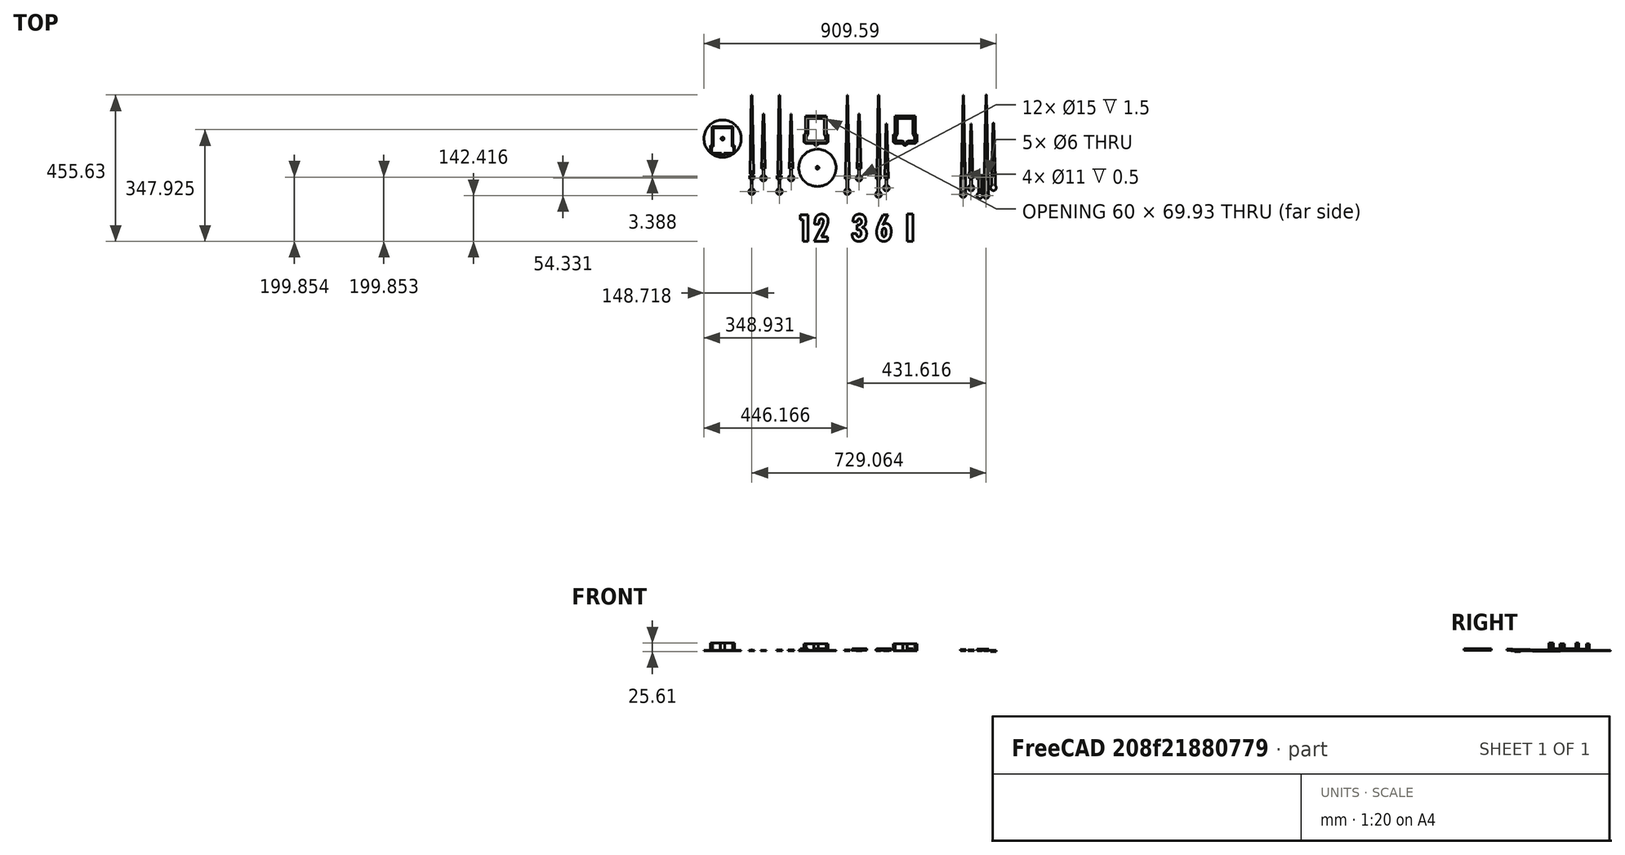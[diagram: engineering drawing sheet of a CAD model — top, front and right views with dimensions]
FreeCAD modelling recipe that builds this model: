
FCSTD DOCUMENT  (FreeCAD 0.20R29177 +426 (Git))
Label: clock
License: All rights reserved
LicenseURL: http://en.wikipedia.org/wiki/All_rights_reserved
objects: Part::Feature×45, Part::Extrusion×39, Part::Part2DObjectPython×38, Part::Cut×15, Part::MultiFuse×14, Part::Refine×9, Part::FeaturePython×7, App::DocumentObjectGroup×4
note: 167 computed .brp shape members not serialized (recipe doc carries the construction recipe); baked Part::Feature solids carry a one-line shape summary decoded from their .brp

FEATURE [Part::Feature] Fusion008002006001002001007001001
  Placement = pos=(-293.726,-1.42e-14,1.78e-14) rot=(0,0,1;0rad)
  shape: bbox 116 x 116 x 24 mm, 36 faces (baked)
FEATURE [Part::Feature] Cut001001004001001  label="clock-hourhand"
  Placement = pos=(267.524,-2.8e-14,0) rot=(0,0,1;0rad)
  shape: bbox 18 x 209 x 2 mm, 16 faces (baked)
FEATURE [Part::Feature] Cut001001007003001001
  Placement = pos=(-86.0924,0,0) rot=(0,0,1;0rad)
  shape: bbox 10.98 x 244.5 x 2.992 mm, 11 faces (baked)
FEATURE [Part::Feature] GrExplode_Slice003_solid001001  label="clock-minutehand-balancer002"
  Placement = pos=(-86.0924,0,0) rot=(0,0,1;0rad)
  shape: bbox 18 x 59.13 x 2 mm, 21 faces (baked)
FEATURE [Part::Feature] Slice002_child0001001  label="Slice002.002"
  shape: bbox 10.98 x 244.5 x 1.996 mm, 11 faces (baked)
FEATURE [Part::Feature] Fusion001001001
  shape: bbox 18 x 59.13 x 2 mm, 22 faces (baked)
FEATURE [Part::Feature] Fusion001001002001
  shape: bbox 18 x 209 x 2.002 mm, 17 faces (baked)
FEATURE [Part::Feature] Slice001_child1001001  label="Slice001.003"
  Placement = pos=(1.29731,-90.7071,-0.5) rot=(0,0,1;0rad)
  shape: bbox 116 x 116 x 1.5 mm, 4 faces (baked)
FEATURE [Part::Feature] Cut001001
  Placement = pos=(-2.79957,33.8928,-1.5) rot=(0,0,1;0rad)
  shape: bbox 75 x 91.93 x 22.5 mm, 43 faces (baked)
FEATURE [Part::Part2DObjectPython] Circle  # Draft 2D object (typed FeaturePython)
  Area = 16.7002
  FirstAngle = 0
  LastAngle = 0
  MakeFace = true
  Placement = pos=(129.41,-196.919,-3.01185) rot=(0,0,1;0rad)
  Radius = 2.30561
FEATURE [Part::Part2DObjectPython] Circle001  # Draft 2D object (typed FeaturePython)
  Area = 46.0771
  FirstAngle = 0
  LastAngle = 0
  MakeFace = true
  Placement = pos=(129.41,-196.919,-3.01185) rot=(0,0,1;0rad)
  Radius = 3.82973
FEATURE [Part::Extrusion] Extrusion
  Base = -> Circle001
  Dir = (0,2.5e-15,-0.597984)
  DirMode = 0
  FaceMakerClass = Part::FaceMakerBullseye
  LengthFwd = 0
  LengthRev = 0
  Solid = true
  Symmetric = false
FEATURE [Part::Extrusion] Extrusion001
  Base = -> Circle
  Dir = (0,2.5e-15,-0.597984)
  DirMode = 0
  FaceMakerClass = Part::FaceMakerBullseye
  LengthFwd = 0
  LengthRev = 0
  Solid = true
  Symmetric = false
FEATURE [Part::Cut] Cut
  Base = -> Extrusion
  Tool = -> Extrusion001
FEATURE [Part::Part2DObjectPython] Rectangle  # Draft 2D object (typed FeaturePython)
  Area = 586.172
  ChamferSize = 0
  Columns = 1
  FilletRadius = 0
  Height = 18.2403
  Length = 32.1361
  MakeFace = true
  Placement = pos=(115.648,-197.225,6.10831) rot=(-1,0,0;1.5708rad)
  Rows = 1
FEATURE [Part::FeaturePython] Slice  # WARN: FeaturePython — macro-defined, semantics opaque (R4)
  Base = -> Cut
  Mode = 1
  Tolerance = 0
  Tools = -> [Rectangle]
FEATURE [Part::FeaturePython] Slice_child1  label="Slice.1"  # WARN: FeaturePython — macro-defined, semantics opaque (R4)
  Base = -> Slice
  FilterType = 1
  Invert = false
  OverrideMaxVal = 0
  WindowFrom = 80
  WindowTo = 100
  items = 1
FEATURE [Part::MultiFuse] Fusion
  Shapes = -> [Fusion001001001,Slice_child1]
FEATURE [App::DocumentObjectGroup] GrExplode_Slice  label="Exploded Slice"
  Group = -> [Fusion]
FEATURE [Part::Refine] Fusion008002006001002001007001002
  Source = -> Fusion
FEATURE [Part::Feature] Fusion008002006001002001007001002001
  shape: bbox 18 x 59.13 x 2 mm, 24 faces (baked)
FEATURE [Part::Part2DObjectPython] Line  # Draft 2D object (typed FeaturePython)
  Area = 0
  ChamferSize = 0
  Closed = false
  End = (123.92,-195.225,-2.60983)
  FilletRadius = 0
  Length = 1
  MakeFace = true
  Placement = pos=(123.92,-195.225,-3.60983) rot=(-1,0,0;1.5708rad)
  Points = (2) [(0,0,0),(0,-1,-2.27374e-13)]
  Start = (123.92,-195.225,-3.60983)
  Subdivisions = 0
FEATURE [Part::Feature] Face
  shape: bbox 14 x 10.13 x 7e-07 mm, 1 faces, 0 solids (baked)
FEATURE [Part::Extrusion] Extrusion002
  Base = -> Face
  Dir = (0,-2e-15,0.402016)
  DirMode = 0
  FaceMakerClass = Part::FaceMakerBullseye
  LengthFwd = 0
  LengthRev = 0
  Solid = true
  Symmetric = false
FEATURE [Part::Feature] Face001
  shape: bbox 18 x 18 x 7e-07 mm, 1 faces, 0 solids (baked)
FEATURE [Part::Extrusion] Extrusion003
  Base = -> Face001
  Dir = (0,0,0.402016)
  DirMode = 0
  FaceMakerClass = Part::FaceMakerBullseye
  LengthFwd = 0
  LengthRev = 0
  Solid = true
  Symmetric = false
FEATURE [Part::MultiFuse] Fusion008002006001002001007001002002
  Shapes = -> [Extrusion002,Extrusion003,Fusion008002006001002001007001002001]
FEATURE [Part::Refine] Fusion008002006001002001007001002002001
  Source = -> Fusion008002006001002001007001002002
FEATURE [Part::Feature] Fusion008002006001002001007001002002001001
  shape: bbox 18 x 59.13 x 2.402 mm, 24 faces (baked)
FEATURE [Part::Feature] Face002
  shape: bbox 18 x 18 x 2e-07 mm, 1 faces, 0 solids (baked)
FEATURE [Part::Extrusion] Extrusion004
  Base = -> Face002
  Dir = (-1e-16,0,0.391829)
  DirMode = 0
  FaceMakerClass = Part::FaceMakerBullseye
  LengthFwd = 0
  LengthRev = 0
  Solid = true
  Symmetric = false
FEATURE [Part::MultiFuse] Fusion008002006001002001007001002002001002
  Shapes = -> [Fusion001001002001,Extrusion004]
FEATURE [Part::Refine] Fusion008002006001002001007001002002001002001
  Source = -> Fusion008002006001002001007001002002001002
FEATURE [Part::Feature] Fusion008002006001002001007001002002001002001001
  shape: bbox 18 x 209 x 2.392 mm, 17 faces (baked)
FEATURE [Part::Feature] Fusion008002006001002001007001002002001002001002
  Placement = pos=(211.355,-1.42e-14,4e-14) rot=(0,0,1;0rad)
  shape: bbox 18 x 59.13 x 2.402 mm, 24 faces (baked)
FEATURE [Part::Feature] Slice002_child0001002  label="Slice002.003"
  Placement = pos=(211.355,-1.42e-14,4e-14) rot=(0,0,1;0rad)
  shape: bbox 10.98 x 244.5 x 1.996 mm, 11 faces (baked)
FEATURE [Part::Feature] Fusion008002006001002001007001002002001002001003
  Placement = pos=(211.355,-1.42e-14,4e-14) rot=(0,0,1;0rad)
  shape: bbox 18 x 209 x 2.392 mm, 17 faces (baked)
FEATURE [Part::Part2DObjectPython] Circle002  # Draft 2D object (typed FeaturePython)
  Area = 38.4845
  FirstAngle = 0
  LastAngle = 0
  MakeFace = true
  Placement = pos=(377.064,-163.449,-3) rot=(0,0,1;0rad)
  Radius = 3.5
FEATURE [Part::Extrusion] Extrusion005
  Base = -> Circle002
  Dir = (0,0,-9.31719)
  DirMode = 0
  FaceMakerClass = Part::FaceMakerBullseye
  LengthFwd = 0
  LengthRev = 0
  Solid = true
  Symmetric = false
FEATURE [Part::Cut] Cut001001007003001002
  Base = -> Fusion008002006001002001007001002002001002001003
  Tool = -> Extrusion005
FEATURE [Part::Part2DObjectPython] Circle003  # Draft 2D object (typed FeaturePython)
  Area = 15.2053
  FirstAngle = 0
  LastAngle = 0
  MakeFace = true
  Placement = pos=(340.766,-184.928,-3.01297) rot=(0,0,1;0rad)
  Radius = 2.2
FEATURE [Part::Extrusion] Extrusion006
  Base = -> Circle003
  Dir = (0,0,-7.79458)
  DirMode = 0
  FaceMakerClass = Part::FaceMakerBullseye
  LengthFwd = 0
  LengthRev = 0
  Solid = true
  Symmetric = false
FEATURE [Part::Cut] Cut001001007003001003
  Base = -> Slice002_child0001002
  Tool = -> Extrusion006
FEATURE [Part::Feature] Face003
  shape: bbox 4.611 x 4.611 x 2e-07 mm, 1 faces, 0 solids (baked)
FEATURE [Part::Extrusion] Extrusion007
  Base = -> Face003
  Dir = (0,0,-0.996429)
  DirMode = 0
  FaceMakerClass = Part::FaceMakerBullseye
  LengthFwd = 0
  LengthRev = 0
  Solid = true
  Symmetric = false
FEATURE [Part::Cut] Cut001001007003001004
  Base = -> Cut001001007003001003
  Tool = -> Extrusion007
FEATURE [Part::Part2DObjectPython] Rectangle001  # Draft 2D object (typed FeaturePython)
  Area = 148.077
  ChamferSize = 0
  Columns = 1
  FilletRadius = 0
  Height = 11.1933
  Length = 13.229
  MakeFace = true
  Placement = pos=(335.406,-182.807,-10.6052) rot=(0.57735,-0.57735,-0.57735;2.0944rad)
  Rows = 1
FEATURE [Part::Part2DObjectPython] Rectangle002  # Draft 2D object (typed FeaturePython)
  Area = 215.213
  ChamferSize = 0
  Columns = 1
  FilletRadius = 0
  Height = 15.7464
  Length = 13.6675
  MakeFace = true
  Placement = pos=(346.125,-182.807,-12.8817) rot=(0.57735,-0.57735,-0.57735;2.0944rad)
  Rows = 1
FEATURE [Part::FeaturePython] Slice001  # WARN: FeaturePython — macro-defined, semantics opaque (R4)
  Base = -> Cut001001007003001004
  Mode = 1
  Tolerance = 0
  Tools = -> [Rectangle002]
FEATURE [Part::FeaturePython] Slice001_child1  label="Slice001.1"  # WARN: FeaturePython — macro-defined, semantics opaque (R4)
  Base = -> Slice001
  FilterType = 1
  Invert = false
  OverrideMaxVal = 0
  WindowFrom = 80
  WindowTo = 100
  items = 1
FEATURE [App::DocumentObjectGroup] GrExplode_Slice001  label="Exploded Slice001"
  Group = -> [Slice001_child1]
FEATURE [Part::FeaturePython] Slice002  # WARN: FeaturePython — macro-defined, semantics opaque (R4)
  Base = -> Slice001_child1
  Mode = 1
  Tolerance = 0
  Tools = -> [Rectangle001]
FEATURE [Part::FeaturePython] Slice002_child0  label="Slice002.0"  # WARN: FeaturePython — macro-defined, semantics opaque (R4)
  Base = -> Slice002
  FilterType = 1
  Invert = false
  OverrideMaxVal = 0
  WindowFrom = 80
  WindowTo = 100
  items = 0
FEATURE [App::DocumentObjectGroup] GrExplode_Slice002  label="Exploded Slice002"
  Group = -> [Slice002_child0]
FEATURE [Part::Part2DObjectPython] Circle004  # Draft 2D object (typed FeaturePython)
  Area = 16.619
  FirstAngle = 0
  LastAngle = 0
  MakeFace = true
  Placement = pos=(340.766,-196.919,-2.60983) rot=(1,0,0;3.14167rad)
  Radius = 2.3
FEATURE [Part::Feature] Face005
  Placement = pos=(211.355,-1.42e-14,4e-14) rot=(0,0,1;0rad)
  shape: bbox 4.694 x 7e-07 x 2.4 mm, 1 faces, 0 solids (baked)
FEATURE [Part::Extrusion] Extrusion008
  Base = -> Face005
  Dir = (1.62e-14,3.80561,9.57e-14)
  DirMode = 0
  FaceMakerClass = Part::FaceMakerBullseye
  LengthFwd = 0
  LengthRev = 0
  Solid = true
  Symmetric = false
FEATURE [Part::Feature] Face006
  Placement = pos=(211.355,-1.42e-14,4e-14) rot=(0,0,1;0rad)
  shape: bbox 4.694 x 7e-07 x 2.4 mm, 1 faces, 0 solids (baked)
FEATURE [Part::Extrusion] Extrusion009
  Base = -> Face006
  Dir = (-1.43e-14,3.80561,4.6e-14)
  DirMode = 0
  FaceMakerClass = Part::FaceMakerBullseye
  LengthFwd = 0
  LengthRev = 0
  Solid = true
  Symmetric = false
FEATURE [Part::Extrusion] Extrusion010
  Base = -> Circle004
  Dir = (-1.407e-13,0.00235422,-31.7358)
  DirMode = 0
  FaceMakerClass = Part::FaceMakerBullseye
  LengthFwd = 0
  LengthRev = 0
  Placement = pos=(5.7e-14,-0.00117711,15.8679) rot=(0,0,1;0rad)
  Solid = true
  Symmetric = false
FEATURE [Part::Feature] Face007
  shape: bbox 7e-07 x 3.806 x 1 mm, 1 faces, 0 solids (baked)
FEATURE [Part::Extrusion] Extrusion011
  Base = -> Face007
  Dir = (-4.61123,1.96e-14,1.3e-15)
  DirMode = 0
  FaceMakerClass = Part::FaceMakerBullseye
  LengthFwd = 0
  LengthRev = 0
  Solid = true
  Symmetric = false
FEATURE [Part::Feature] Face008
  Placement = pos=(211.355,-1.42e-14,4e-14) rot=(0,0,1;0rad)
  shape: bbox 7e-07 x 2 x 1 mm, 1 faces, 0 solids (baked)
FEATURE [Part::Extrusion] Extrusion012
  Base = -> Face008
  Dir = (-4.61123,1.3e-14,-1.25e-14)
  DirMode = 0
  FaceMakerClass = Part::FaceMakerBullseye
  LengthFwd = 0
  LengthRev = 0
  Solid = true
  Symmetric = false
FEATURE [Part::MultiFuse] Fusion008002006001002001007001002002001002001004
  Shapes = -> [Extrusion012,Extrusion011,Extrusion008,Extrusion009,Fusion008002006001002001007001002002001002001002]
FEATURE [Part::Part2DObjectPython] Circle005  # Draft 2D object (typed FeaturePython)
  Area = 95.0332
  FirstAngle = 0
  LastAngle = 0
  MakeFace = true
  Placement = pos=(340.766,-196.919,-2.60983) rot=(0,0,1;0rad)
  Radius = 5.5
FEATURE [Part::Cut] Cut001001007003001005
  Base = -> Fusion008002006001002001007001002002001002001004
  Tool = -> Extrusion010
FEATURE [Part::Extrusion] Extrusion013
  Base = -> Circle005
  Dir = (0,2.5e-15,-0.5)
  DirMode = 0
  FaceMakerClass = Part::FaceMakerBullseye
  LengthFwd = 0
  LengthRev = 0
  Solid = true
  Symmetric = false
FEATURE [Part::Cut] Cut001001007003001006
  Base = -> Cut001001007003001005
  Tool = -> Extrusion013
FEATURE [Part::Refine] Cut001001007003001006001
  Source = -> Cut001001007003001006
FEATURE [Part::Feature] Face009
  shape: bbox 14 x 7e-07 x 2.4 mm, 1 faces, 0 solids (baked)
FEATURE [Part::Extrusion] Extrusion014
  Base = -> Face009
  Dir = (1.3e-15,0.4,5.7e-15)
  DirMode = 0
  FaceMakerClass = Part::FaceMakerBullseye
  LengthFwd = 0
  LengthRev = 0
  Solid = true
  Symmetric = false
FEATURE [Part::MultiFuse] Fusion008002006001002001007001002002001002001005
  Shapes = -> [Extrusion014,Cut001001007003001006001]
FEATURE [Part::Part2DObjectPython] Line004  # Draft 2D object (typed FeaturePython)
  Area = 0
  ChamferSize = 0
  Closed = false
  End = (346.256,-191.019,-2.60983)
  FilletRadius = 0
  Length = 1
  MakeFace = true
  Placement = pos=(346.256,-191.019,-3.60983) rot=(-1,0,0;1.5708rad)
  Points = (2) [(0,0,0),(0,-1,1.13687e-13)]
  Start = (346.256,-191.019,-3.60983)
  Subdivisions = 0
FEATURE [Part::Part2DObjectPython] Line005  # Draft 2D object (typed FeaturePython)
  Area = 0
  ChamferSize = 0
  Closed = false
  End = (335.275,-191.019,-2.60983)
  FilletRadius = 0
  Length = 1
  MakeFace = true
  Placement = pos=(335.275,-191.019,-3.60983) rot=(-1,0,0;1.5708rad)
  Points = (2) [(0,0,0),(0,-1,1.13687e-13)]
  Start = (335.275,-191.019,-3.60983)
  Subdivisions = 0
FEATURE [Part::Part2DObjectPython] Line007  # Draft 2D object (typed FeaturePython)
  Area = 0
  ChamferSize = 0
  Closed = false
  End = (333.766,-196.918,-2.60983)
  FilletRadius = 0
  Length = 6.08928
  MakeFace = true
  Placement = pos=(335.275,-191.019,-2.60983) rot=(0,0,1;0rad)
  Points = (2) [(0,0,0),(-1.50938,-5.89925,-4.08562e-14)]
  Start = (335.275,-191.019,-2.60983)
  Subdivisions = 0
FEATURE [Part::Part2DObjectPython] Line009  # Draft 2D object (typed FeaturePython)
  Area = 0
  ChamferSize = 0
  Closed = false
  End = (346.256,-191.019,-2.60983)
  FilletRadius = 0
  Length = 6.08928
  MakeFace = true
  Placement = pos=(347.766,-196.918,-2.60983) rot=(0,0,1;0rad)
  Points = (2) [(0,0,0),(-1.50937,5.89925,3.55271e-15)]
  Start = (347.766,-196.918,-2.60983)
  Subdivisions = 0
FEATURE [Part::Part2DObjectPython] Wire  # Draft 2D object (typed FeaturePython)
  Area = 4.45209
  ChamferSize = 0
  Closed = true
  End = (333.766,-191.019,-2.60983)
  FilletRadius = 0
  Length = 13.4979
  MakeFace = true
  Placement = pos=(333.766,-196.918,-2.60983) rot=(0,0,1;0rad)
  Points = (3) [(0,0,0),(1.50938,5.89925,4.17444e-14),(0,5.89925,2.66454e-14)]
  Start = (333.766,-196.918,-2.60983)
  Subdivisions = 0
FEATURE [Part::Extrusion] Extrusion015
  Base = -> Wire
  Dir = (1.197e-13,1.354e-13,-11.1843)
  DirMode = 0
  FaceMakerClass = Part::FaceMakerBullseye
  LengthFwd = 0
  LengthRev = 0
  Solid = true
  Symmetric = false
FEATURE [Part::Cut] Cut001001007003001006002
  Base = -> Fusion008002006001002001007001002002001002001005
  Tool = -> Extrusion015
FEATURE [Part::Part2DObjectPython] Wire001  # Draft 2D object (typed FeaturePython)
  Area = 4.45209
  ChamferSize = 0
  Closed = true
  End = (347.766,-191.019,-2.60983)
  FilletRadius = 0
  Length = 13.4979
  MakeFace = true
  Placement = pos=(347.766,-196.918,-2.60983) rot=(0,0,1;0rad)
  Points = (3) [(0,0,0),(-1.50937,5.89925,4.44089e-15),(0,5.89925,-2.22045e-15)]
  Start = (347.766,-196.918,-2.60983)
  Subdivisions = 0
FEATURE [Part::Extrusion] Extrusion016
  Base = -> Wire001
  Dir = (-6.82e-14,1.324e-13,-18.3507)
  DirMode = 0
  FaceMakerClass = Part::FaceMakerBullseye
  LengthFwd = 0
  LengthRev = 0
  Solid = true
  Symmetric = false
FEATURE [Part::Cut] Cut001001007003001006003
  Base = -> Cut001001007003001006002
  Tool = -> Extrusion016
FEATURE [Part::Part2DObjectPython] Rectangle003  # Draft 2D object (typed FeaturePython)
  Area = 74.4926
  ChamferSize = 0
  Columns = 1
  FilletRadius = 0
  Height = 2.48841
  Length = 29.9358
  MakeFace = true
  Placement = pos=(322.609,-190.33,-5.00983) rot=(1,0,0;3.14159rad)
  Rows = 1
FEATURE [Part::Extrusion] Extrusion017
  Base = -> Rectangle003
  Dir = (-1e-15,-1e-15,1.4)
  DirMode = 0
  FaceMakerClass = Part::FaceMakerBullseye
  LengthFwd = 0
  LengthRev = 0
  Solid = true
  Symmetric = false
FEATURE [Part::Cut] Cut001001007003001006004
  Base = -> Cut001001007003001006003
  Tool = -> Extrusion017
FEATURE [Part::Refine] Slice002_child0001003  label="Slice002.004"
  Source = -> Slice002_child0
FEATURE [Part::Refine] Cut001001007003001006004001
  Source = -> Cut001001007003001006004
FEATURE [Part::Part2DObjectPython] Circle006  # Draft 2D object (typed FeaturePython)
  Area = 15.2053
  FirstAngle = 0
  LastAngle = 0
  MakeFace = true
  Placement = pos=(340.766,-184.928,-4.0094) rot=(1,0,0;7.4e-05rad)
  Radius = 2.2
FEATURE [Part::Part2DObjectPython] Circle007  # Draft 2D object (typed FeaturePython)
  Area = 78.5398
  FirstAngle = 0
  LastAngle = 0
  MakeFace = true
  Placement = pos=(340.766,-184.928,-4.0094) rot=(1,0,0;7.4e-05rad)
  Radius = 5
FEATURE [Part::Part2DObjectPython] Circle008  # Draft 2D object (typed FeaturePython)
  Area = 28.2743
  FirstAngle = 0
  LastAngle = 0
  MakeFace = true
  Placement = pos=(340.766,-196.918,-3.10983) rot=(0,0,1;0rad)
  Radius = 3
FEATURE [Part::Extrusion] Extrusion020
  Base = -> Circle008
  Dir = (1e-16,2.86e-14,-5.71518)
  DirMode = 0
  FaceMakerClass = Part::FaceMakerBullseye
  LengthFwd = 0
  LengthRev = 0
  Solid = true
  Symmetric = false
FEATURE [Part::Cut] Cut001001007003001006004003
  Base = -> Cut001001007003001006004001
  Tool = -> Extrusion020
FEATURE [Part::Part2DObjectPython] Wire003  # Draft 2D object (typed FeaturePython)
  Area = 1509.1
  ChamferSize = 0
  Closed = true
  End = (341.766,54.5638,-3.99126)
  FilletRadius = 0
  Length = 487.383
  MakeFace = true
  Placement = pos=(346.125,-182.728,-4.00924) rot=(1,0,0;7.4e-05rad)
  Points = (4) [(0,0,0),(-10.7193,8.52651e-14,-3.77476e-14),(-6.35968,237.292,0.000371511),(-4.35968,237.292,0.000371511)]
  Start = (346.125,-182.728,-4.00924)
  Subdivisions = 0
FEATURE [Part::Extrusion] Extrusion021
  Base = -> Wire003
  Dir = (-5.3e-15,7.56942e-05,-0.999295)
  DirMode = 0
  FaceMakerClass = Part::FaceMakerBullseye
  LengthFwd = 0
  LengthRev = 0
  Solid = true
  Symmetric = false
FEATURE [Part::Part2DObjectPython] Rectangle006  # Draft 2D object (typed FeaturePython)
  Area = 77.266
  ChamferSize = 0
  Columns = 1
  FilletRadius = 0
  Height = 7.2081
  Length = 10.7193
  MakeFace = true
  Placement = pos=(335.406,-189.936,-4.0094) rot=(1,0,0;7.6e-05rad)
  Rows = 1
FEATURE [Part::Extrusion] Extrusion022
  Base = -> Rectangle006
  Dir = (-5.3e-15,7.57232e-05,-0.999678)
  DirMode = 0
  FaceMakerClass = Part::FaceMakerBullseye
  LengthFwd = 0
  LengthRev = 0
  Solid = true
  Symmetric = false
FEATURE [Part::Part2DObjectPython] Circle009  # Draft 2D object (typed FeaturePython)
  Area = 15.2053
  FirstAngle = 0
  LastAngle = 0
  MakeFace = true
  Placement = pos=(340.766,-184.928,-4.0094) rot=(1,0,0;7.6e-05rad)
  Radius = 2.2
FEATURE [Part::Extrusion] Extrusion023
  Base = -> Circle009
  Dir = (-3.72e-14,0.000537769,-7.09948)
  DirMode = 0
  FaceMakerClass = Part::FaceMakerBullseye
  LengthFwd = 0
  LengthRev = 0
  Placement = pos=(5.7e-14,-0.000268884,3.54974) rot=(0,0,1;0rad)
  Solid = true
  Symmetric = false
FEATURE [Part::MultiFuse] Fusion008002006001002001007001002002001002001007
  Shapes = -> [Extrusion021,Extrusion022]
FEATURE [Part::Cut] Cut001001007003001006004004
  Base = -> Fusion008002006001002001007001002002001002001007
  Tool = -> Extrusion023
FEATURE [Part::Part2DObjectPython] Circle010  # Draft 2D object (typed FeaturePython)
  Area = 28.2743
  FirstAngle = 0
  LastAngle = 0
  MakeFace = true
  Placement = pos=(340.766,-184.928,-4.00902) rot=(1,0,0;7.6e-05rad)
  Radius = 3
FEATURE [Part::Extrusion] Extrusion024
  Base = -> Circle010
  Dir = (-1.6e-15,2.27487e-05,-0.300322)
  DirMode = 0
  FaceMakerClass = Part::FaceMakerBullseye
  LengthFwd = 0
  LengthRev = 0
  Solid = true
  Symmetric = false
FEATURE [Part::Cut] Cut001001007003001006004005
  Base = -> Cut001001007003001006004004
  Tool = -> Extrusion024
FEATURE [Part::Refine] Cut001001007003001006004005001
  Source = -> Cut001001007003001006004005
FEATURE [Part::Part2DObjectPython] Circle011  # Draft 2D object (typed FeaturePython)
  Area = 30.1907
  FirstAngle = 0
  LastAngle = 0
  MakeFace = true
  Placement = pos=(340.766,-184.928,-4.00902) rot=(1,0,0;7.6e-05rad)
  Radius = 3.1
FEATURE [Part::Extrusion] Extrusion025
  Base = -> Circle011
  Dir = (-1.6e-15,2.27487e-05,-0.300322)
  DirMode = 0
  FaceMakerClass = Part::FaceMakerBullseye
  LengthFwd = 0
  LengthRev = 0
  Solid = true
  Symmetric = false
FEATURE [Part::Cut] Cut001001007003001006004005002
  Base = -> Cut001001007003001006004005001
  Tool = -> Extrusion025
FEATURE [Part::Part2DObjectPython] Circle012  # Draft 2D object (typed FeaturePython)
  Area = 39.5919
  FirstAngle = 0
  LastAngle = 0
  MakeFace = true
  Placement = pos=(377.064,-163.449,-4.00083) rot=(0,0,1;0rad)
  Radius = 3.55
FEATURE [Part::Extrusion] Extrusion026
  Base = -> Circle012
  Dir = (6.1e-15,1.6e-15,-19.7391)
  DirMode = 0
  FaceMakerClass = Part::FaceMakerBullseye
  LengthFwd = 0
  LengthRev = 0
  Solid = true
  Symmetric = false
FEATURE [Part::Cut] Cut001001007003001006004005003
  Base = -> Cut001001007003001002
  Tool = -> Extrusion026
FEATURE [Part::Feature] Cut001001007003001006004005003001  label="HourHand"
  shape: bbox 18 x 209 x 2.392 mm, 15 faces (baked)
FEATURE [Part::Feature] Cut001001007003001006004005002001  label="MinuteHand"
  shape: bbox 10.72 x 244.5 x 1.018 mm, 15 faces (baked)
FEATURE [Part::Feature] Cut001001007003001006004003001  label="MinuteHand-Balance"
  shape: bbox 18 x 63.34 x 2.402 mm, 25 faces (baked)
FEATURE [Part::Feature] Fusion008002006001002001007001002002001002001008  label="HourHand.v2"
  Placement = pos=(85.2168,-30.8568,1.38283) rot=(0,0,1;0rad)
  shape: bbox 18 x 209 x 2.392 mm, 14 faces (baked)
FEATURE [Part::Feature] Fusion008002006001002001007001002002001002001009  label="MinuteHand-Balance.v2"
  Placement = pos=(96.782,0,6.6e-14) rot=(0,0,1;0rad)
  shape: bbox 18 x 72.34 x 3.801 mm, 25 faces (baked)
FEATURE [Part::Feature] Cut001001007003001006004005003002  label="MinuteHand.v2"
  Placement = pos=(97.1955,-0.0933249,-0.000752062) rot=(0,0,1;0rad)
  shape: bbox 10.72 x 244.5 x 1.018 mm, 15 faces (baked)
FEATURE [Part::Feature] Cut001001007003001006004005003004_solid001001  label="Cut001001007003001006004005003004 (Solid)002"
  Placement = pos=(276.655,-2.8e-14,-6.9e-14) rot=(0,0,1;0rad)
  shape: bbox 73.5 x 91.93 x 21.5 mm, 45 faces (baked)
FEATURE [App::DocumentObjectGroup] Draft_Construction  label="Construction"
FEATURE [Part::Part2DObjectPython] ShapeString  # Draft 2D object (typed FeaturePython)
  FontFile = /run/user/1000/doc/f5ed1d15/Futura Bold font.ttf
  MakeFace = true
  Placement = pos=(183.377,-400.159,-3.5) rot=(0,0,1;0rad)
  Size = 93
  String = 12
  Tracking = 0
FEATURE [Part::Part2DObjectPython] ShapeString001  # Draft 2D object (typed FeaturePython)
  FontFile = /run/user/1000/doc/f5ed1d15/Futura Bold font.ttf
  MakeFace = true
  Placement = pos=(183.377,-486.508,-3.5) rot=(0,0,1;0rad)
  Size = 93
  String = 3
  Tracking = 0
FEATURE [Part::Part2DObjectPython] Line012  # Draft 2D object (typed FeaturePython)
  Area = 0
  ChamferSize = 0
  Closed = false
  End = (528.923,-400.159,-3.5)
  FilletRadius = 0
  Length = 350
  MakeFace = true
  Placement = pos=(178.923,-400.159,-3.5) rot=(0,0,1;0rad)
  Points = (2) [(0,0,0),(350,0,0)]
  Start = (178.923,-400.159,-3.5)
  Subdivisions = 0
FEATURE [Part::Part2DObjectPython] Rectangle007  # Draft 2D object (typed FeaturePython)
  Area = 1599.7
  ChamferSize = 0
  Columns = 1
  FilletRadius = 0
  Height = 85
  Length = 18.82
  MakeFace = true
  Placement = pos=(377.158,-400.159,-3.5) rot=(0,0,1;0rad)
  Rows = 1
FEATURE [Part::Extrusion] Extrusion027
  Base = -> ShapeString
  Dir = (0,0,3)
  DirMode = 0
  FaceMakerClass = Part::FaceMakerBullseye
  LengthFwd = 0
  LengthRev = 0
  Solid = true
  Symmetric = false
FEATURE [Part::Extrusion] Extrusion028
  Base = -> ShapeString001
  Dir = (0,0,3)
  DirMode = 0
  FaceMakerClass = Part::FaceMakerBullseye
  LengthFwd = 0
  LengthRev = 0
  Placement = pos=(169.403,86.3489,0) rot=(0,0,1;0rad)
  Solid = true
  Symmetric = false
FEATURE [Part::Extrusion] Extrusion029
  Base = -> Rectangle007
  Dir = (0,0,3)
  DirMode = 0
  FaceMakerClass = Part::FaceMakerBullseye
  LengthFwd = 0
  LengthRev = 0
  Placement = pos=(149.284,7.3953e-11,0) rot=(0,0,1;0rad)
  Solid = true
  Symmetric = false
FEATURE [Part::Part2DObjectPython] ShapeString002  # Draft 2D object (typed FeaturePython)
  FontFile = /run/user/1000/doc/f5ed1d15/Futura Bold font.ttf
  MakeFace = true
  Placement = pos=(183.377,-486.508,-3.5) rot=(0,0,1;0rad)
  Size = 93
  String = 6
  Tracking = 0
FEATURE [Part::Extrusion] Extrusion030
  Base = -> ShapeString002
  Dir = (0,0,3)
  DirMode = 0
  FaceMakerClass = Part::FaceMakerBullseye
  LengthFwd = 0
  LengthRev = 0
  Placement = pos=(245.378,86.3489,0) rot=(0,0,1;0rad)
  Solid = true
  Symmetric = false
FEATURE [Part::Feature] Fusion008002006001002001007001002002001002001010001001
  Placement = pos=(263.433,-1.42e-14,-1.4331e-12) rot=(0,0,1;0rad)
  shape: bbox 10.72 x 244.5 x 2.012 mm, 20 faces, 2 solids (baked)
FEATURE [Part::Feature] Fusion008002006001002001007001002002001002001010001002  label="HourHand.v003"
  Placement = pos=(348.65,-30.8568,1.38283) rot=(0,0,1;0rad)
  shape: bbox 18 x 209 x 2.392 mm, 14 faces (baked)
FEATURE [Part::Feature] Fusion008002006001002001007001002002001002001011001001
  Placement = pos=(263.433,-1.42e-14,-1.4331e-12) rot=(0,0,1;0rad)
  shape: bbox 18 x 72.34 x 3.801 mm, 25 faces (baked)
FEATURE [Part::Part2DObjectPython] Line013  # Draft 2D object (typed FeaturePython)
  Area = 0
  ChamferSize = 0
  Closed = false
  End = (528.923,-315.159,-3.5)
  FilletRadius = 0
  Length = 350
  MakeFace = true
  Placement = pos=(178.923,-315.159,-3.5) rot=(1,0,0;3.14159rad)
  Points = (2) [(0,0,0),(350,0,0)]
  Start = (178.923,-315.159,-3.5)
  Subdivisions = 0
FEATURE [Part::Part2DObjectPython] Line014  # Draft 2D object (typed FeaturePython)
  Area = 0
  ChamferSize = 0
  Closed = false
  End = (693.981,-205.356,-3.60865)
  FilletRadius = 0
  Length = 3.57911
  MakeFace = true
  Placement = pos=(697.56,-205.356,-3.60865) rot=(1,0,0;1.5708rad)
  Points = (2) [(0,0,0),(-3.57911,0,-9.37916e-13)]
  Start = (697.56,-205.356,-3.60865)
  Subdivisions = 0
FEATURE [Part::Part2DObjectPython] Rectangle008  # Draft 2D object (typed FeaturePython)
  Area = 3.57487
  ChamferSize = 0
  Columns = 1
  FilletRadius = 0
  Height = 0.998815
  Length = 3.57911
  MakeFace = true
  Placement = pos=(693.981,-205.356,-3.60865) rot=(1,0,0;1.5708rad)
  Rows = 1
FEATURE [Part::Extrusion] Extrusion031
  Base = -> Rectangle008
  Dir = (-1.5e-15,-49,1.632e-13)
  DirMode = 0
  FaceMakerClass = Part::FaceMakerBullseye
  LengthFwd = 0
  LengthRev = 0
  Solid = true
  Symmetric = false
FEATURE [Part::FeaturePython] Clone  label="Extrusion032"  # Draft clone (typed FeaturePython)
  AttacherType = Attacher::AttachEngine3D
  Fuse = false
  Objects = -> [Extrusion031]
  Placement = pos=(10.4209,1.8758e-12,9e-16) rot=(0,0,1;0rad)
  Scale = (1,1,1)
FEATURE [Part::Part2DObjectPython] Circle013  # Draft 2D object (typed FeaturePython)
  Area = 176.715
  FirstAngle = 0
  LastAngle = 0
  MakeFace = true
  Placement = pos=(700.981,-254.356,-3.61066) rot=(1,0,0;3.14159rad)
  Radius = 7.5
FEATURE [Part::Extrusion] Extrusion032  label="Extrusion033"
  Base = -> Circle013
  Dir = (-2e-16,3.48e-14,10.4699)
  DirMode = 0
  FaceMakerClass = Part::FaceMakerBullseye
  LengthFwd = 0
  LengthRev = 0
  Solid = true
  Symmetric = false
FEATURE [Part::MultiFuse] Fusion008002006001002001007001002002001002001011001002
  Shapes = -> [Extrusion031,Clone]
FEATURE [Part::Cut] Cut001001007003001006004005003003
  Base = -> Fusion008002006001002001007001002002001002001011001002
  Tool = -> Extrusion032
FEATURE [Part::MultiFuse] Fusion008002006001002001007001002002001002001011001003
  Shapes = -> [Fusion008002006001002001007001002002001002001011001001,Cut001001007003001006004005003003]
FEATURE [Part::Refine] Fusion008002006001002001007001002002001002001011001003001
  Source = -> Fusion008002006001002001007001002002001002001011001003
FEATURE [Part::Refine] Fusion008002006001002001007001002002001002001011001003001001
  Source = -> Fusion008002006001002001007001002002001002001011001003001
FEATURE [Part::Feature] Fusion008002006001002001007001002002001002001011001003001001001
  shape: bbox 18 x 72.34 x 3.801 mm, 23 faces (baked)
FEATURE [Part::Feature] Fusion008002006001002001007001002002001002001011001003001001004002001
  shape: bbox 18 x 209 x 2.399 mm, 17 faces (baked)
FEATURE [Part::Feature] Fusion008002006001002001007001002002001002001011001003001001004002002
  Placement = pos=(334.95,-1.42e-14,-1.4331e-12) rot=(0,0,1;0rad)
  shape: bbox 10.72 x 244.5 x 2.012 mm, 20 faces, 2 solids (baked)
FEATURE [Part::Feature] Fusion008002006001002001007001002002001002001011001003001001002
  Placement = pos=(71.401,-3.38756,-0.00109799) rot=(0,0,1;0rad)
  shape: bbox 18 x 72.34 x 4.801 mm, 37 faces (baked)
FEATURE [Part::Feature] Fusion008002006001002001007001002002001002001011001003001001003001
  Placement = pos=(-19.4776,0,-1.8e-14) rot=(0,0,1;0rad)
  shape: bbox 18 x 72.34 x 4.801 mm, 25 faces (baked)
FEATURE [Part::Part2DObjectPython] Circle014  # Draft 2D object (typed FeaturePython)
  Area = 3.14159
  FirstAngle = 0
  LastAngle = 0
  MakeFace = true
  Placement = pos=(772.911,54.4705,-3.99202) rot=(1,0,0;7.6e-05rad)
  Radius = 1
FEATURE [Part::Extrusion] Extrusion033  label="Extrusion034"
  Base = -> Circle014
  Dir = (-4.8e-15,7.56942e-05,-0.999295)
  DirMode = 0
  FaceMakerClass = Part::FaceMakerBullseye
  LengthFwd = 0
  LengthRev = 0
  Solid = true
  Symmetric = false
FEATURE [Part::MultiFuse] Fusion008002006001002001007001002002001002001011001003001001004002003
  Shapes = -> [Fusion008002006001002001007001002002001002001011001003001001004002002,Extrusion033]
FEATURE [Part::Part2DObjectPython] Circle015  # Draft 2D object (typed FeaturePython)
  Area = 3.14159
  FirstAngle = 0
  LastAngle = 0
  MakeFace = true
  Placement = pos=(795.193,-33.1148,-4.01114) rot=(0,0,1;0rad)
  Radius = 1
FEATURE [Part::Extrusion] Extrusion034  label="Extrusion035"
  Base = -> Circle015
  Dir = (2e-16,1e-16,-0.99917)
  DirMode = 0
  FaceMakerClass = Part::FaceMakerBullseye
  LengthFwd = 0
  LengthRev = 0
  Solid = true
  Symmetric = false
FEATURE [Part::MultiFuse] Fusion008002006001002001007001002002001002001011001003001001004002004
  Shapes = -> [Fusion008002006001002001007001002002001002001011001003001001004002001,Extrusion034]
FEATURE [Part::Feature] Face010
  Placement = pos=(-2.03727,1.1908,-1.40048) rot=(0,0,1;0rad)
  shape: bbox 18 x 18 x 2e-07 mm, 1 faces, 0 solids (baked)
FEATURE [Part::Extrusion] Extrusion035  label="Extrusion036"
  Base = -> Face010
  Dir = (0,0,-0.2)
  DirMode = 0
  FaceMakerClass = Part::FaceMakerBullseye
  LengthFwd = 0
  LengthRev = 0
  Solid = true
  Symmetric = false
FEATURE [Part::MultiFuse] Fusion008002006001002001007001002002001002001011001003001001004002005
  Shapes = -> [Fusion008002006001002001007001002002001002001011001003001001004002004,Extrusion035]
FEATURE [Part::Part2DObjectPython] Line015  # Draft 2D object (typed FeaturePython)
  Area = 0
  ChamferSize = 0
  Closed = false
  End = (545.263,-400.159,1.5)
  FilletRadius = 0
  Length = 5
  MakeFace = true
  Placement = pos=(545.263,-400.159,-3.5) rot=(1,0,0;1.5708rad)
  Points = (2) [(0,0,0),(0,5,0)]
  Start = (545.263,-400.159,-3.5)
  Subdivisions = 0
FEATURE [Part::Feature] Face011
  Placement = pos=(526.443,-400.159,-0.5) rot=(0,0,1;0rad)
  shape: bbox 18.82 x 85 x 2e-07 mm, 1 faces, 0 solids (baked)
FEATURE [Part::Extrusion] Extrusion036  label="Extrusion037"
  Base = -> Face011
  Dir = (0,0,2)
  DirMode = 0
  FaceMakerClass = Part::FaceMakerBullseye
  LengthFwd = 0
  LengthRev = 0
  Solid = true
  Symmetric = false
FEATURE [Part::MultiFuse] Fusion008002006001002001007001002002001002001011001003001001004002006
  Shapes = -> [Extrusion029,Extrusion036]
FEATURE [Part::Feature] Face012
  Placement = pos=(428.755,-400.159,-0.5) rot=(0,0,1;0rad)
  shape: bbox 45.38 x 82.43 x 2e-07 mm, 1 faces, 0 solids (baked)
FEATURE [Part::Extrusion] Extrusion037  label="Extrusion038"
  Base = -> Face012
  Dir = (0,0,2)
  DirMode = 0
  FaceMakerClass = Part::FaceMakerBullseye
  LengthFwd = 0
  LengthRev = 0
  Solid = true
  Symmetric = false
FEATURE [Part::Feature] Face013
  Placement = pos=(352.78,-400.159,-0.5) rot=(0,0,1;0rad)
  shape: bbox 45.27 x 84.86 x 2e-07 mm, 1 faces, 0 solids (baked)
FEATURE [Part::Extrusion] Extrusion038  label="Extrusion039"
  Base = -> Face013
  Dir = (0,0,2)
  DirMode = 0
  FaceMakerClass = Part::FaceMakerBullseye
  LengthFwd = 0
  LengthRev = 0
  Solid = true
  Symmetric = false
FEATURE [Part::Feature] Face014
  Placement = pos=(183.377,-400.159,-0.5) rot=(0,0,1;0rad)
  shape: bbox 43.07 x 84.86 x 2e-07 mm, 1 faces, 0 solids (baked)
FEATURE [Part::Extrusion] Extrusion039  label="Extrusion040"
  Base = -> Face014
  Dir = (0,0,2)
  DirMode = 0
  FaceMakerClass = Part::FaceMakerBullseye
  LengthFwd = 0
  LengthRev = 0
  Solid = true
  Symmetric = false
FEATURE [Part::Feature] Face015
  Placement = pos=(183.377,-400.159,-0.5) rot=(0,0,1;0rad)
  shape: bbox 23.79 x 82.43 x 2e-07 mm, 1 faces, 0 solids (baked)
FEATURE [Part::Extrusion] Extrusion040  label="Extrusion041"
  Base = -> Face015
  Dir = (0,0,2)
  DirMode = 0
  FaceMakerClass = Part::FaceMakerBullseye
  LengthFwd = 0
  LengthRev = 0
  Solid = true
  Symmetric = false
FEATURE [Part::MultiFuse] Fusion008002006001002001007001002002001002001011001003001001004002009
  Shapes = -> [Extrusion028,Extrusion038]
FEATURE [Part::MultiFuse] Fusion008002006001002001007001002002001002001011001003001001004002010
  Shapes = -> [Extrusion030,Extrusion037]
